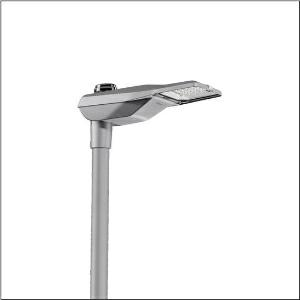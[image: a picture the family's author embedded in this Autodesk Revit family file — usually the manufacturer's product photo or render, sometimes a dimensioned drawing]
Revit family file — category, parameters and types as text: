
# Revit family: streetlight_sl_21_micro___st1_0a_5xe5d37n08cb_defe
name_source: partatom
category: Lighting Fixtures
units: mm (PartAtom-declared; Revit-internal decimal feet)

## family parameters
Cut with Voids When Loaded = No
Host = Face
Light Source = No
Part Type = Normal
Room Calculation Point = No
Round Connector Dimension = Use Diameter
Shared = No

## types (1)
- --- (1 x LED, 2290 lm, 15.8 W, 3000K)
    Apparent Load = 16 VA
    CIE Flux Codes = 37 72 97 100 100
    Color Rendering = 70
    Color Temperature = 3000K
    Default Elevation = 1800 mm
    Description = Streetlight SL 21 micro, mast luminaire, primary light control with lens, of PMMA, primary optical cover: cover, of toughened safety glass, transparent, light distribution: ST1.0a, light emission: direct distribution, primary light characteristic: asymmetric, installation type: post-top, LED, 3G 1.5mm², High Power LED, rated luminous flux: 2.290lm, luminous efficacy: 145lm/W, light colour: 730, colour temperature: 3000K, control: overheat protection, pre-setting: linear dimming characteristic, constant luminous flux control, time-dependent luminous flux control, flexible luminous flux parameterisation, mains connection: 230..240V, AC, 50/60Hz, connection cable pre-assembled, cable length: 6,5m, wiring characteristics: H07RN-F, start of lifetime: 16W, end of service life: 16W, reduction: 8W, luminaire housing, of diecast aluminium (EN AC-44300), powder-coated, Siteco® metallic grey (DB 702S), corrosivity category C5 mid according to DIN EN ISO 12944, multi-level sealing system, sealing non-destructively replaceable, inclination adjustable: 0°, 5°, 10°, 15°, length: 528mm, width: 235mm, height: 110mm, spigot size: 76/60mm (post-top), protection rating (complete): IP66, insulation class (complete): insulation class I (protective earthing), certification: CE, ENEC, ENEC+, VDE, impact resistance: IK09, permissible operating ambient temperature for outdoor applications: -40..+50°C, standard-compliant lighting for roads and squares, packaging unit: 1 piece

Light Distribution: ST1.0a
    Height = 110 mm
    Lamp = 1 x LED
    Lamp Light Flux = 2290 lm
    Lamp Power = 15.8 W
    Lamp count = 1
    Length = 528 mm
    Luminous efficacy = 145 lm/W
    Manufacturer = Siteco
    ModVariant = No
    Model = 5XE5D37N08CB
    Number of Poles = 1
    OnlyDefault = Yes
    Power Factor = 1
    Product Name = Streetlight SL 21 micro | ST1.0a
    Product group = mast luminaire | pylon top
    ProductGroupID = 6100
    Protection Class = Protection class I
    Protection Degree = IP 66
    RLX_Detail_Level = 1
    RLX_Emergency_Light_Flux = 0 lm
    RLX_Emergency_Type = 0
    RLX_Emergency_Type_DB = No
    RlxData = <blob elided: 98557 chars, md5=7c755cdc>
    Socket = socket
    Standby Power = 0 W
    System Light Flux = 2290 lm
    System Power = 16 W
    Type Comments = factory setting: luminous flux: 100 % | dim-lin: 254 | 300 mA
    Type Image = l_1294375.jpg
    URL = http://relux.com
    VarID = @adj_106387
    Voltage = 0 V
    Weight = 0.00 kg
    Width = 235 mm

## geometry (parser evidence)
native form markers: Blend x4, Sweep x11
no freeform markers — native parametric forms only
